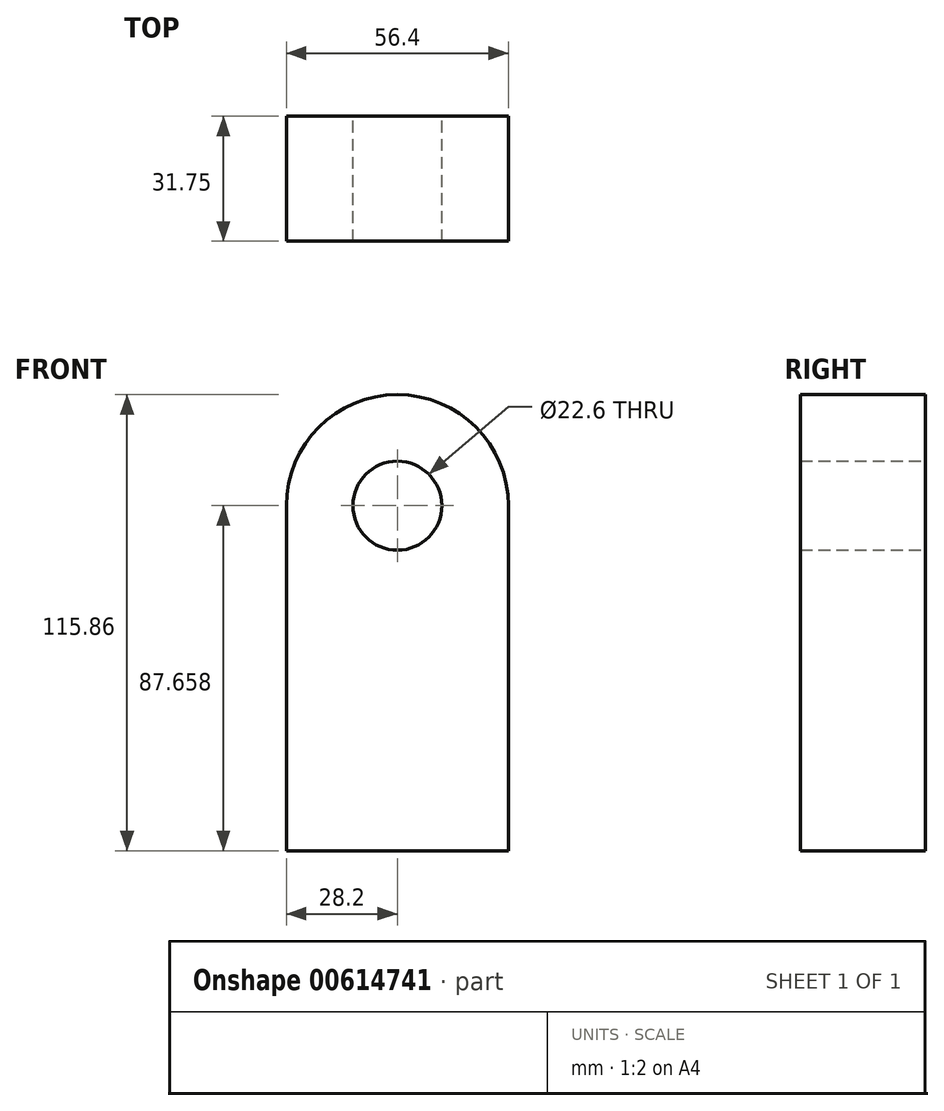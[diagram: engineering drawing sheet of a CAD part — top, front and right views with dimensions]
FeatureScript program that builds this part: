
annotation { "Feature Type Name" : "Feature", "Feature Type Description" : "" }
export const myFeature = defineFeature(function(context is Context, id is Id, definition is map)
    precondition{}
    {
        {
            var Q0;
            Q0=qCreatedBy(makeId("Front.planeOp"),FACE);
            var sketch = newSketch(context, id + "F0", { "sketchPlane" : qUnion([Q0])});
            skLineSegment(sketch, "E0.bottom", {"start": v(28.2, -43.83) * mm, "end": v(-28.2, -43.83) * mm});
            skLineSegment(sketch, "E0.left", {"start": v(28.2, -43.83) * mm, "end": v(28.2, 43.83) * mm});
            skLineSegment(sketch, "E0.right", {"start": v(-28.2, -43.83) * mm, "end": v(-28.2, 43.83) * mm});
            skPoint(sketch, "E0.middle", {"position": v(0, 0) * mm});
            skArc(sketch, "E1", {"start": v(28.2, 43.83) * mm, "mid": v(0, 72.03) * mm, "end": v(-28.2, 43.83) * mm});
            skCircle(sketch, "E2", {"center": v(0, 43.83) * mm, "radius": 11.3 * mm});
            skSolve(sketch);
        }
        {
            var Q0;
            Q0=makeQuery(id+"F0.imprint","IMPRINT",FACE,{"disambiguationData":[TD([[makeQuery(id+"F0.imprint","IMPRINT",EDGE,{"derivedFrom":sQuery(id+"F0.wireOp",EDGE,"E0.bottom")}),-1.0]])]});
            extrude(context, id + "F1", {"entities" : qUnion([Q0]), "depth" : 31.75 * mm, "offsetDistance" : 25.4 * mm});
        }
    });
